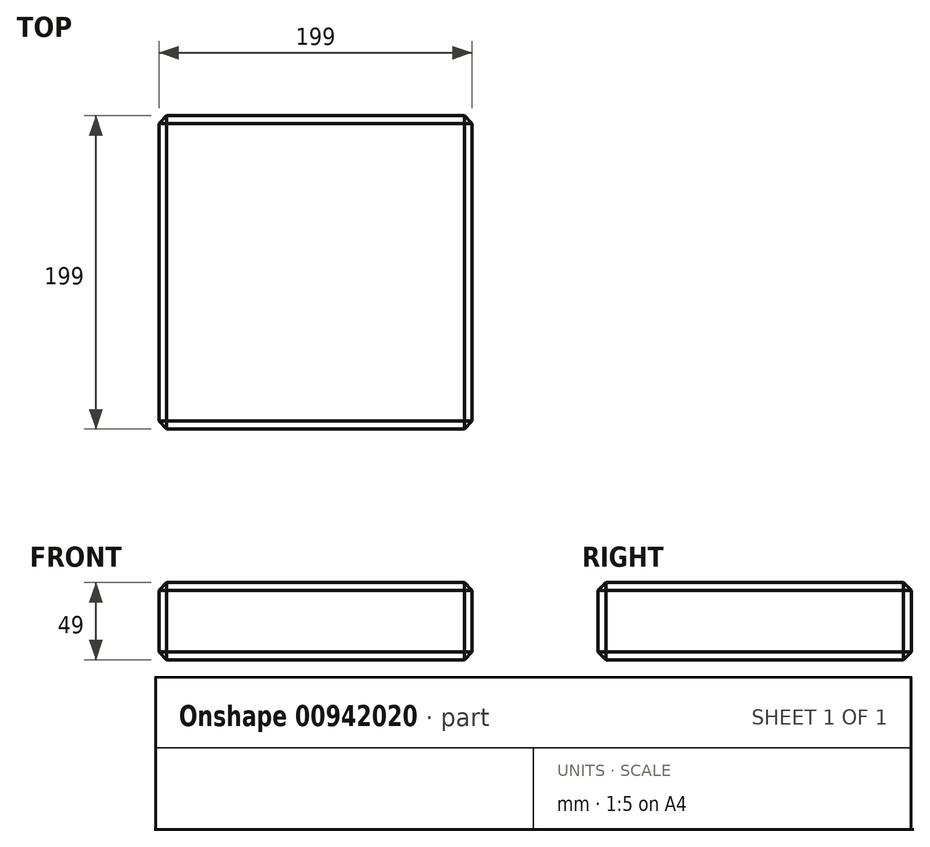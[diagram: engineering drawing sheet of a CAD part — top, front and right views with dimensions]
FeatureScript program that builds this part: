
annotation { "Feature Type Name" : "Feature", "Feature Type Description" : "" }
export const myFeature = defineFeature(function(context is Context, id is Id, definition is map)
    precondition{}
    {
        {
            var Q0;
            Q0=qCreatedBy(makeId("Front.planeOp"),FACE);
            var sketch = newSketch(context, id + "F0", { "sketchPlane" : qUnion([Q0])});
            skLineSegment(sketch, "E0.bottom", {"start": v(99.5, -24.5) * mm, "end": v(-99.5, -24.5) * mm});
            skLineSegment(sketch, "E0.top", {"start": v(99.5, 24.5) * mm, "end": v(-99.5, 24.5) * mm});
            skLineSegment(sketch, "E0.left", {"start": v(99.5, -24.5) * mm, "end": v(99.5, 24.5) * mm});
            skLineSegment(sketch, "E0.right", {"start": v(-99.5, -24.5) * mm, "end": v(-99.5, 24.5) * mm});
            skPoint(sketch, "E0.middle", {"position": v(0, 0) * mm});
            skSolve(sketch);
        }
        {
            var Q0;
            Q0=makeQuery(id+"F0.imprint","IMPRINT",FACE,{"disambiguationData":[TD([[makeQuery(id+"F0.imprint","IMPRINT",EDGE,{"derivedFrom":sQuery(id+"F0.wireOp",EDGE,"E0.bottom")}),-1.0]])]});
            extrude(context, id + "F1", {"entities" : qUnion([Q0]), "depth" : 199 * mm, "offsetDistance" : 25.4 * mm});
        }
        {
            var Q0;
            Q0=makeQuery(id+"F1.opExtrude","SWEPT_EDGE",EDGE,{"disambiguationData":[OSD([sQuery(id+"F0.wireOp",EDGE,"E0.top"),sQuery(id+"F0.wireOp",EDGE,"E0.left")])]});
            var Q1;
            Q1=makeQuery(id+"F1.opExtrude","CAP_EDGE",EDGE,{"disambiguationData":[OSD([sQuery(id+"F0.wireOp",EDGE,"E0.top")])],"isStart":false});
            var Q2;
            Q2=makeQuery(id+"F1.opExtrude","CAP_EDGE",EDGE,{"disambiguationData":[OSD([sQuery(id+"F0.wireOp",EDGE,"E0.left")])],"isStart":false});
            var Q3;
            Q3=makeQuery(id+"F1.opExtrude","CAP_EDGE",EDGE,{"disambiguationData":[OSD([sQuery(id+"F0.wireOp",EDGE,"E0.bottom")])],"isStart":false});
            var Q4;
            Q4=makeQuery(id+"F1.opExtrude","CAP_EDGE",EDGE,{"disambiguationData":[OSD([sQuery(id+"F0.wireOp",EDGE,"E0.right")])],"isStart":false});
            var Q5;
            Q5=makeQuery(id+"F1.opExtrude","SWEPT_EDGE",EDGE,{"disambiguationData":[OSD([sQuery(id+"F0.wireOp",EDGE,"E0.bottom"),sQuery(id+"F0.wireOp",EDGE,"E0.right")])]});
            var Q6;
            Q6=makeQuery(id+"F1.opExtrude","SWEPT_EDGE",EDGE,{"disambiguationData":[OSD([sQuery(id+"F0.wireOp",EDGE,"E0.top"),sQuery(id+"F0.wireOp",EDGE,"E0.right")])]});
            var Q7;
            Q7=makeQuery(id+"F1.opExtrude","CAP_EDGE",EDGE,{"disambiguationData":[OSD([sQuery(id+"F0.wireOp",EDGE,"E0.right")])],"isStart":true});
            var Q8;
            Q8=makeQuery(id+"F1.opExtrude","CAP_EDGE",EDGE,{"disambiguationData":[OSD([sQuery(id+"F0.wireOp",EDGE,"E0.top")])],"isStart":true});
            var Q9;
            Q9=makeQuery(id+"F1.opExtrude","CAP_EDGE",EDGE,{"disambiguationData":[OSD([sQuery(id+"F0.wireOp",EDGE,"E0.bottom")])],"isStart":true});
            var Q10;
            Q10=makeQuery(id+"F1.opExtrude","CAP_EDGE",EDGE,{"disambiguationData":[OSD([sQuery(id+"F0.wireOp",EDGE,"E0.left")])],"isStart":true});
            var Q11;
            Q11=makeQuery(id+"F1.opExtrude","SWEPT_EDGE",EDGE,{"disambiguationData":[OSD([sQuery(id+"F0.wireOp",EDGE,"E0.bottom"),sQuery(id+"F0.wireOp",EDGE,"E0.left")])]});
            chamfer(context, id + "F2", {"entities" : qUnion([Q0, Q1, Q2, Q3, Q4, Q5, Q6, Q7, Q8, Q9, Q10, Q11]), "width" : 5 * mm, "tangentPropagation" : true});
        }
    });
